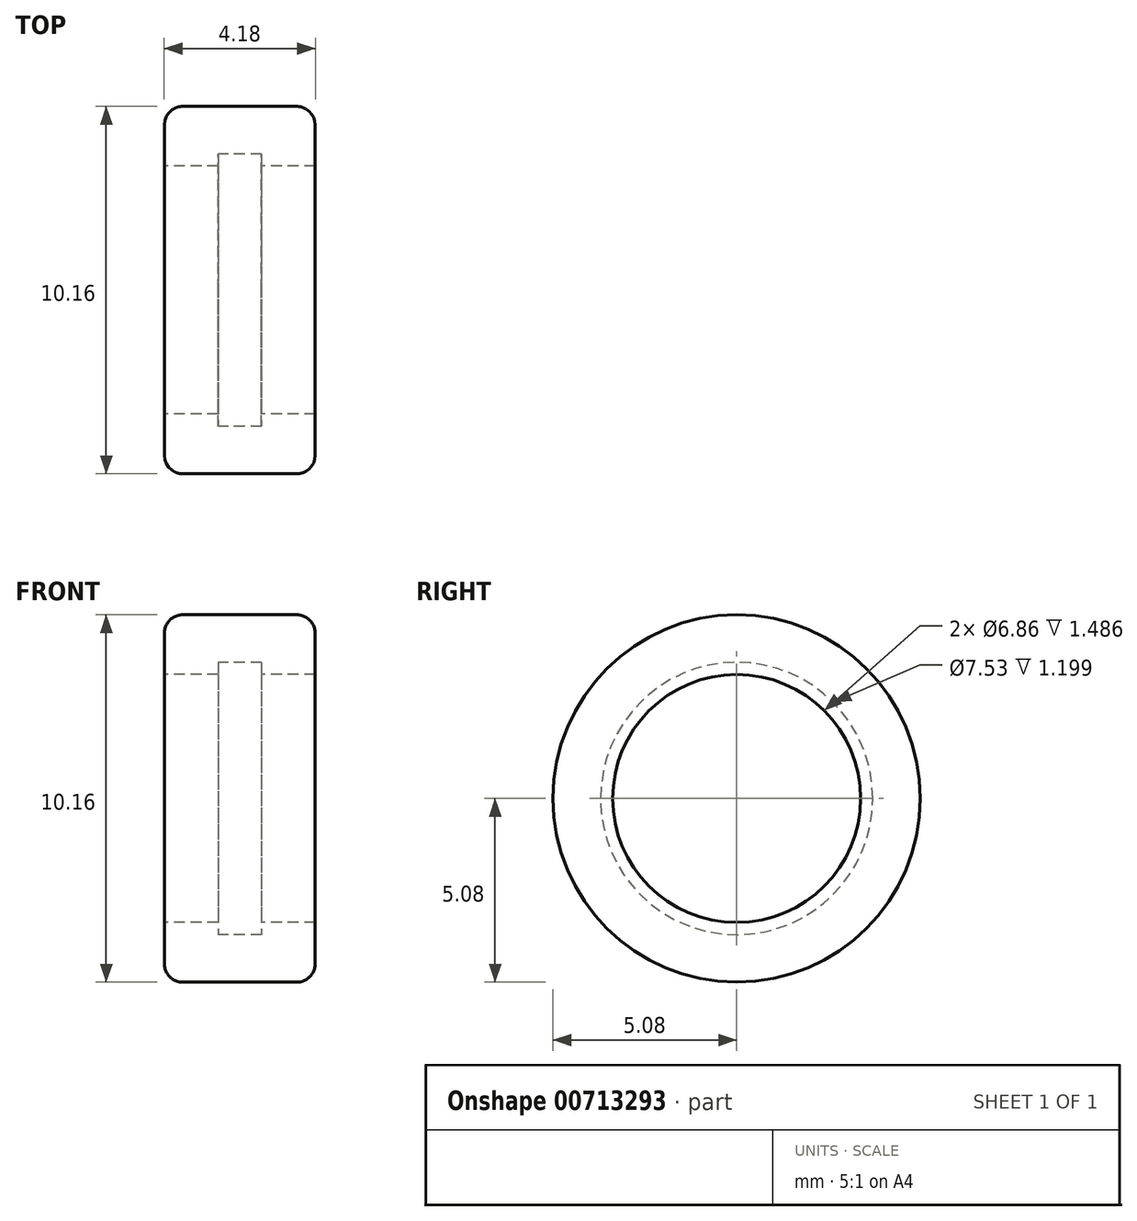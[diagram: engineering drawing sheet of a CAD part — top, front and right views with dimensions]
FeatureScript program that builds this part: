
annotation { "Feature Type Name" : "Feature", "Feature Type Description" : "" }
export const myFeature = defineFeature(function(context is Context, id is Id, definition is map)
    precondition{}
    {
        {
            var Q0;
            Q0=qCreatedBy(makeId("Front.planeOp"),FACE);
            var sketch = newSketch(context, id + "F0", { "sketchPlane" : qUnion([Q0])});
            skLineSegment(sketch, "E0.bottom", {"start": v(-2.09, 5.08) * mm, "end": v(2.09, 5.08) * mm});
            skLineSegment(sketch, "E0.top", {"start": v(-2.09, -5.08) * mm, "end": v(2.09, -5.08) * mm});
            skLineSegment(sketch, "E0.left", {"start": v(-2.09, 5.08) * mm, "end": v(-2.09, -5.08) * mm});
            skLineSegment(sketch, "E0.right", {"start": v(2.09, 5.08) * mm, "end": v(2.09, -5.08) * mm});
            skPoint(sketch, "E0.middle", {"position": v(0, 0) * mm});
            skLineSegment(sketch, "E1", {"start": v(-2.09, 0) * mm, "end": v(2.09, 0) * mm});
            skLineSegment(sketch, "E2", {"start": v(-2.09, 3.43) * mm, "end": v(-0.6, 3.43) * mm});
            skLineSegment(sketch, "E3.bottom", {"start": v(-0.6, 3.76) * mm, "end": v(0.6, 3.76) * mm});
            skLineSegment(sketch, "E3.left", {"start": v(-0.6, 3.76) * mm, "end": v(-0.6, 3.43) * mm});
            skLineSegment(sketch, "E3.right", {"start": v(0.6, 3.76) * mm, "end": v(0.6, 3.43) * mm});
            skPoint(sketch, "E3.middle", {"position": v(0, 3.43) * mm});
            skPoint(sketch, "E4.orphan", {"position": v(0.6, 3.1) * mm});
            skLineSegment(sketch, "E5.trimOffspring", {"start": v(0.6, 3.43) * mm, "end": v(2.09, 3.43) * mm});
            skPoint(sketch, "E6.orphan", {"position": v(-0.6, 3.1) * mm});
            skLineSegment(sketch, "E7.MirrorCS", {"start": v(0.6, -3.43) * mm, "end": v(2.09, -3.43) * mm});
            skLineSegment(sketch, "E8.MirrorCS", {"start": v(0.6, -3.76) * mm, "end": v(0.6, -3.43) * mm});
            skLineSegment(sketch, "E9.MirrorCS", {"start": v(-0.6, -3.76) * mm, "end": v(0.6, -3.76) * mm});
            skLineSegment(sketch, "E10.MirrorCS", {"start": v(-0.6, -3.76) * mm, "end": v(-0.6, -3.43) * mm});
            skLineSegment(sketch, "E11.MirrorCS", {"start": v(-2.09, -3.43) * mm, "end": v(-0.6, -3.43) * mm});
            skSolve(sketch);
        }
        {
            var Q0;
            {var subQ1=sQuery(id+"F0.wireOp",EDGE,"E0.bottom");Q0=makeQuery(id+"F0.imprint","IMPRINT",FACE,{"disambiguationData":[TD([[makeQuery(id+"F0.imprint","IMPRINT",EDGE,{"derivedFrom":subQ1}),-1.0]])]});}
            var Q1;
            Q1=sQuery(id+"F0.wireOp",EDGE,"E1");
            revolve(context, id + "F1", {"surfaceOperationType" : NewSurfaceOperationType.NEW, "entities" : qUnion([Q0]), "axis" : qUnion([Q1]), "revolveType" : RevolveType.FULL});
        }
        {
            var Q0;
            Q0=makeQuery(id+"F1.opRevolve","SWEPT_EDGE",EDGE,{"disambiguationData":[OSD([sQuery(id+"F0.wireOp",EDGE,"E0.bottom"),sQuery(id+"F0.wireOp",EDGE,"E0.left")])]});
            var Q1;
            Q1=makeQuery(id+"F1.opRevolve","SWEPT_EDGE",EDGE,{"disambiguationData":[OSD([sQuery(id+"F0.wireOp",EDGE,"E0.bottom"),sQuery(id+"F0.wireOp",EDGE,"E0.right")])]});
            fillet(context, id + "F2", {"entities" : qUnion([Q0, Q1]), "radius" : 0.5 * mm, "tangentPropagation" : true, "allowEdgeOverflow" : false});
        }
    });
